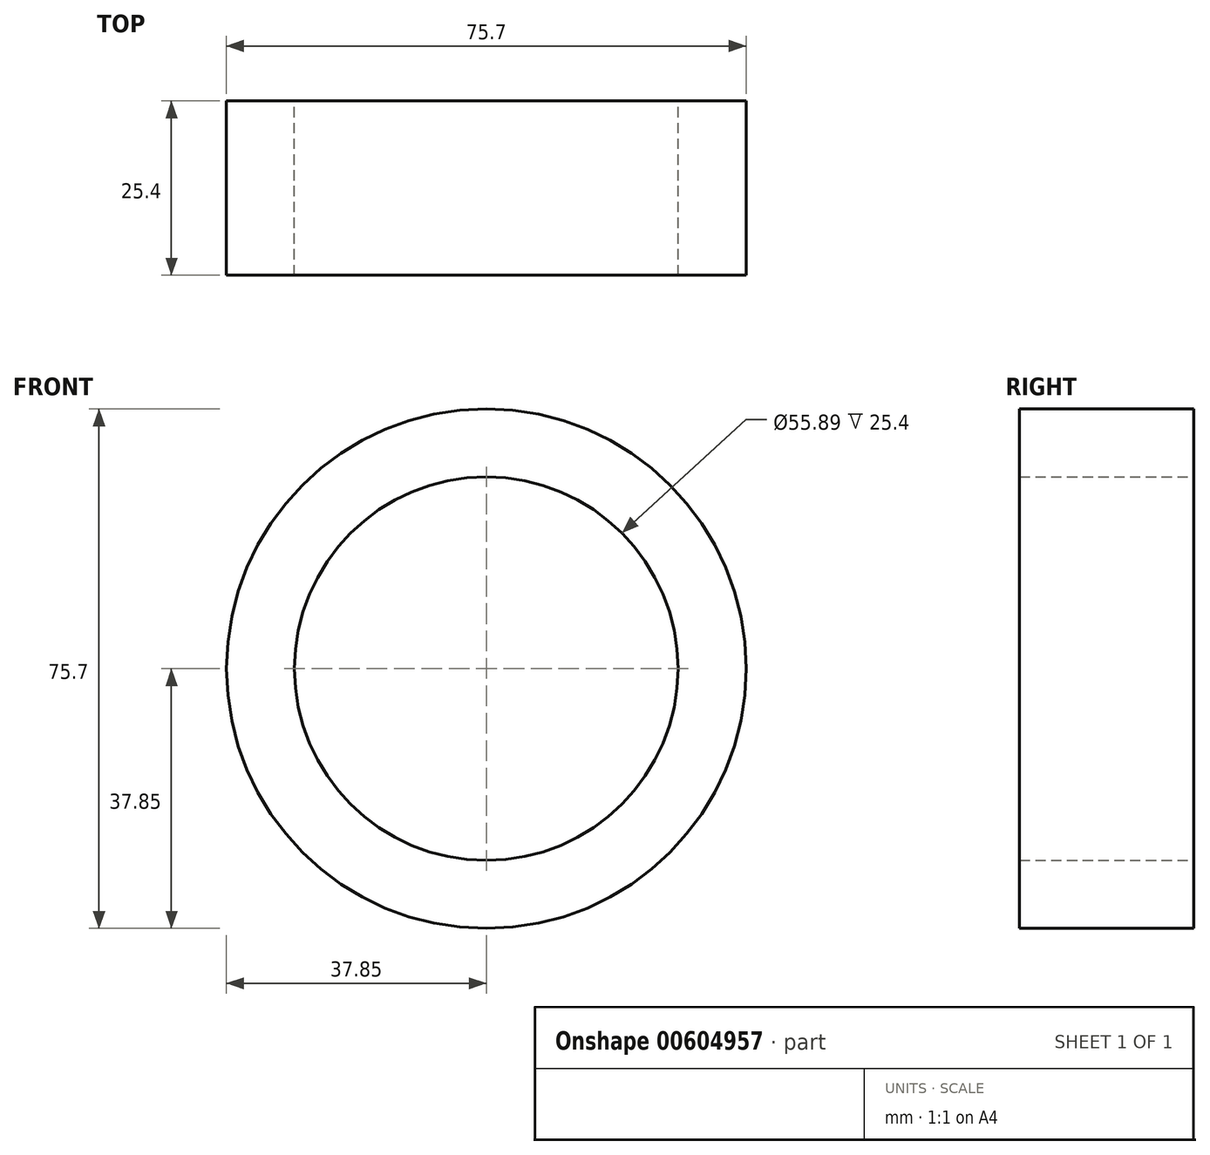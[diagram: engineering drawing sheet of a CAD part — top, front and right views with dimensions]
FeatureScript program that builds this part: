
annotation { "Feature Type Name" : "Feature", "Feature Type Description" : "" }
export const myFeature = defineFeature(function(context is Context, id is Id, definition is map)
    precondition{}
    {
        {
            var Q0;
            Q0=qCreatedBy(makeId("Front.planeOp"),FACE);
            var sketch = newSketch(context, id + "F0", { "sketchPlane" : qUnion([Q0])});
            skCircle(sketch, "E0", {"center": v(0, 0) * mm, "radius": 37.85 * mm});
            skCircle(sketch, "E1.0", {"center": v(0, 0) * mm, "radius": 27.95 * mm});
            skSolve(sketch);
        }
        {
            var Q0;
            Q0=makeQuery(id+"F0.imprint","IMPRINT",FACE,{"disambiguationData":[TD([[makeQuery(id+"F0.imprint","IMPRINT",EDGE,{"derivedFrom":sQuery(id+"F0.wireOp",EDGE,"E0")}),1.0]])]});
            extrude(context, id + "F1", {"entities" : qUnion([Q0]), "depth" : 25.4 * mm, "offsetDistance" : 25.4 * mm});
        }
        {
            var Q0;
            Q0=makeQuery(id+"F1.opExtrude","CAP_FACE",FACE,{"disambiguationData":[OSD([sQuery(id+"F0.wireOp",EDGE,"E0"),sQuery(id+"F0.wireOp",EDGE,"E1.0")])],"isStart":false});
            var sketch = newSketch(context, id + "F2", { "sketchPlane" : qUnion([Q0])});
            skCircle(sketch, "E2.0", {"center": v(0, 0) * mm, "radius": 37.85 * mm});
            skCircle(sketch, "E3.0", {"center": v(0, 0) * mm, "radius": 27.95 * mm});
            skLineSegment(sketch, "E4", {"start": v(0, 27.95) * mm, "end": v(5, 37.52) * mm});
            skLineSegment(sketch, "E5", {"start": v(5, 37.52) * mm, "end": v(-5, 37.52) * mm});
            skLineSegment(sketch, "E6", {"start": v(-5, 37.52) * mm, "end": v(0, 27.95) * mm});
            skSolve(sketch);
        }
    });
